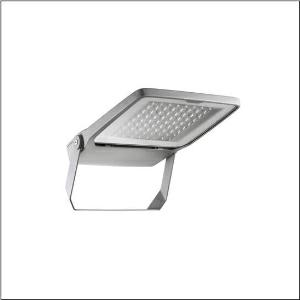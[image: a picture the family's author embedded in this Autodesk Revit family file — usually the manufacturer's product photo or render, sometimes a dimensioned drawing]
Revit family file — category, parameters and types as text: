
# Revit family: floodlight_fl_20_mini___rs17_5xa7672c1b1ac_bda3
name_source: partatom
category: Lighting Fixtures
units: mm (PartAtom-declared; Revit-internal decimal feet)

## family parameters
Cut with Voids When Loaded = No
Host = Face
Light Source = No
Part Type = Normal
Room Calculation Point = No
Round Connector Dimension = Use Diameter
Shared = No

## types (1)
- --- (1 x LED 3000K / CRI = 80 (unbekannt), 10480 lm, 3000K)
    Apparent Load = 96 VA
    CIE Flux Codes = 79 92 99 100 100
    Color Rendering = 80
    Color Temperature = 3000K
    Default Elevation = 1800 mm
    Description = Floodlight FL 20 mini, floodlight, primary light control with lens, of plastic, primary optical cover: protective disc, of toughened safety glass, transparent, light distribution: RS17, light emission: direct distribution, primary light characteristic: rotationally symmetric, installation type: surface-mounted, LED, High Power LED, rated luminous flux: 10.480lm, luminous efficacy: 109lm/W, light colour: 830, colour temperature: 3000K, control gear: ECG Plus, control: flexible luminous flux parameterisation, time-dependent luminous flux control, digital communication interface, power reduction, overheat protection, electronic power reduction, with terminal, 5-pole, max. 2.5mm², mains connection: 220..240V, AC, 50/60Hz, rated input power: 96W, LED unit, of diecast aluminium, powder-coated, Siteco® metallic grey (DB 702S), corrosivity category C5 mid according to DIN EN ISO 12944, incl. 1x M20 cable gland for cable Ø 6.5..12mm, length: 446mm, width: 355mm, height: 62mm, housing frame, of diecast aluminium, powder-coated, Siteco® metallic grey (DB 702S), mounting bracket, of steel, powder-coated, Siteco® metallic grey (DB 702S), DALI, protection rating (complete): IP66, insulation class (complete): insulation class II (safety insulation), certification: CE, ENEC, VDE, protection symbol: D, permissible operating ambient temperature: -40..+40°C, permissible operating ambient temperature for outdoor applications: -40..+50°C, standard: DIN EN 12944, packaging unit: 1 piece

Light Distribution: RS17
    Height = 62 mm  [stored 0.203412 ft]
    Lamp = 1 x LED 3000K / CRI >= 80 (unbekannt)
    Lamp Light Flux = 10480 lm
    Lamp count = 1
    Length = 467 mm
    Luminous efficacy = 109 lm/W
    Manufacturer = Siteco
    ModVariant = No
    Model = 5XA7672C1B1AC
    Mounting Place = Wall
    Mounting Type = Surface mounted
    Number of Poles = 1
    OnlyDefault = Yes
    Power Factor = 1
    Product Name = Floodlight FL 20 mini | RS17
    Product group = floodlight | wall mounted
    ProductGroupID = 2001
    Protection Class = Protection class II
    Protection Degree = IP 66
    RLX_Detail_Level = 1
    RLX_Emergency_Light_Flux = 0 lm
    RLX_Emergency_Type = 0
    RLX_Emergency_Type_DB = No
    RlxData = <blob elided: 68997 chars, md5=6b4a826e>
    Socket = socket
    Standby Power = 0 W
    System Light Flux = 10480 lm
    System Power = 96 W
    Type Comments = factory setting: luminous flux: 100 % | dim-lin: 254 | 500 mA
    Type Image = l_1005948.jpg
    URL = http://relux.com
    VarID = @adj_163049
    Voltage = 0 V
    Weight = 0.00 kg
    Width = 335 mm

note: [stored X ft] marks values corroborated as IEEE doubles in the binary element streams (Revit-internal decimal feet)

## geometry (parser evidence)
native form markers: Blend x4, Sweep x10
no freeform markers — native parametric forms only
